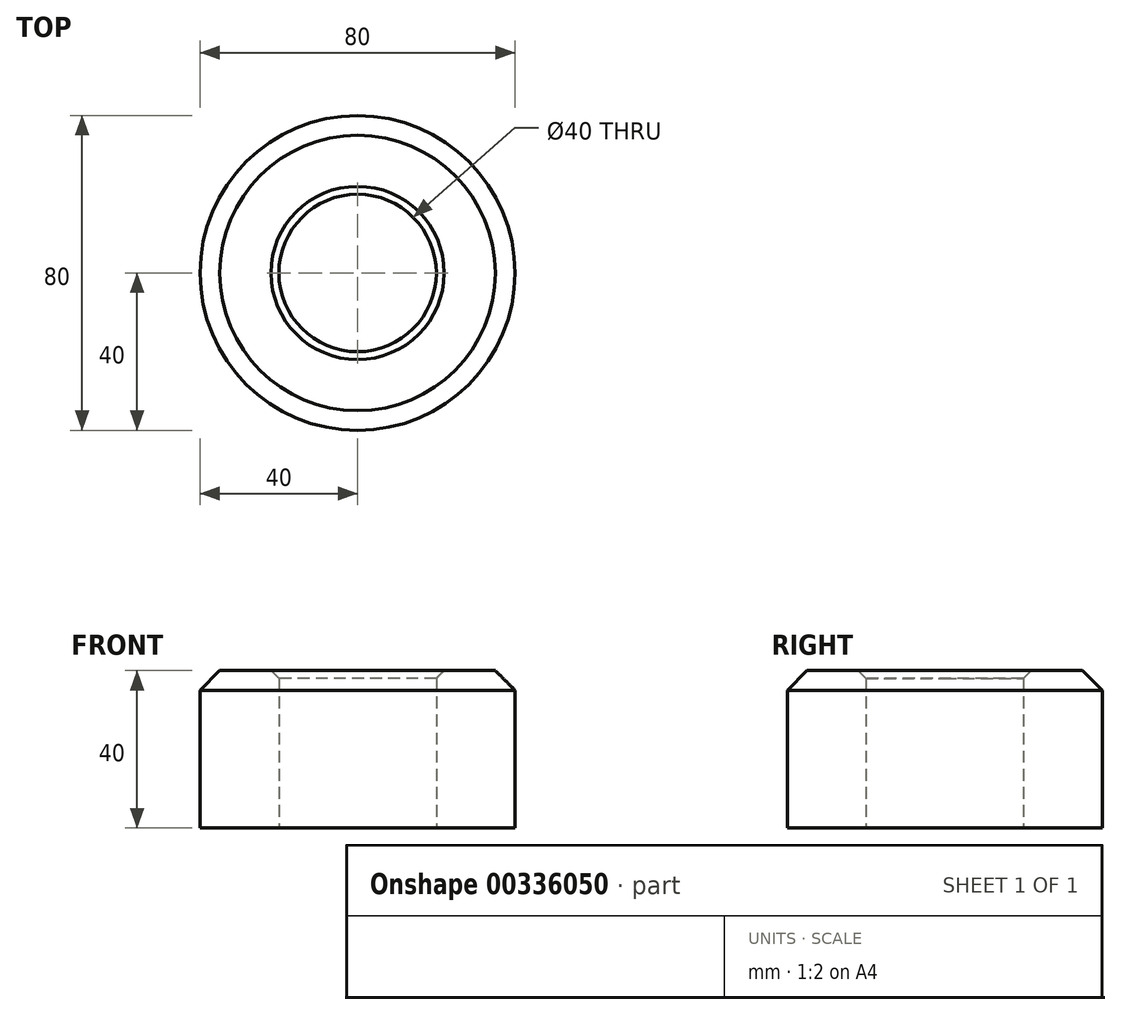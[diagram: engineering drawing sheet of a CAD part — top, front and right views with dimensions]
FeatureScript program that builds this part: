
annotation { "Feature Type Name" : "Feature", "Feature Type Description" : "" }
export const myFeature = defineFeature(function(context is Context, id is Id, definition is map)
    precondition{}
    {
        {
            var Q0;
            Q0=qCreatedBy(makeId("Top.planeOp"),FACE);
            var sketch = newSketch(context, id + "F0", { "sketchPlane" : qUnion([Q0])});
            skCircle(sketch, "E0", {"center": v(0, 0) * mm, "radius": 40 * mm});
            skCircle(sketch, "E1", {"center": v(0, 0) * mm, "radius": 20 * mm});
            skSolve(sketch);
        }
        {
            var Q0;
            Q0=makeQuery(id+"F0.imprint","IMPRINT",FACE,{"disambiguationData":[TD([[makeQuery(id+"F0.imprint","IMPRINT",EDGE,{"derivedFrom":sQuery(id+"F0.wireOp",EDGE,"E0")}),1.0]])]});
            extrude(context, id + "F1", {"entities" : qUnion([Q0]), "depth" : 40 * mm});
        }
        {
            var Q0;
            Q0=makeQuery(id+"F1.opExtrude","CAP_EDGE",EDGE,{"disambiguationData":[OSD([sQuery(id+"F0.wireOp",EDGE,"E0")])],"isStart":false});
            chamfer(context, id + "F2", {"entities" : qUnion([Q0]), "width" : 5 * mm, "tangentPropagation" : true});
        }
        {
            var Q0;
            Q0=makeQuery(id+"F1.opExtrude","CAP_EDGE",EDGE,{"disambiguationData":[OSD([sQuery(id+"F0.wireOp",EDGE,"E1")])],"isStart":false});
            chamfer(context, id + "F3", {"entities" : qUnion([Q0]), "width" : 2 * mm, "tangentPropagation" : true});
        }
    });
